# Revit family: Domotics-DomesticRanges-GEWISS-SYSTEM_COMMAND-TWO-WAY_SWITCH_2M
name_source: partatom
category: Apparecchi elettrici
revit_build: Autodesk Revit 2016 (Build: 20161004_0715(x64)
units: mm (PartAtom-declared; Revit-internal decimal feet)

## family parameters
Condiviso = Sì
Host = Superficie
Mantenere orientamento annotazione = Sì
Numero OmniClass = 23.80.50.11.14
Punto di calcolo locali = Sì
Quota connettore circolare = Usa diametro
Taglio con vuoti quando caricato = No
Tipo di parte = Normale
Titolo OmniClass = Switches

## types (2) — shared parameters
Button key = With diffuser
Carico apparente = 0 VA
Catalogue = DOMOTICS
Catalogue Range = SYSTEM - DOMESTIC RANGE
Description. = Two-way switch
Description: = 1P - 16 AX - illuminable
Electrocod = 0130
IDF = 81d0e624-9eec-47de-a259-0ae64e065f3d
IDT = 48717bbd-d383-42eb-95bb-567ea7826302
Immagine tipo = GW21589.jpg
Larghezza pulsante = 46 mm  [stored 0.150919 ft]
N. poli = 1
No. SYSTEM modules = 2
Produttore = GEWISS S.p.A.
Prospetto di default = 1219 mm
SEO = 2 way switch
Simbolo = SIMBOLO DEVIATORI : DEV1P
Technical sheet = https://www.gewiss.com
Tipo_ = SYSTEM DEVIATORI 2M_BASE : Nero
Type = Two-way switch
URL = https://www.gewiss.com
Version file RFA = 19.4
Volt = 230 V
Voltage = 250 V ac
Voltage: = 250 V ac

## per-type parameters (varying)
| type | Colour | Descrizione | EAN code | Modello |
| GW21589 - Black | Black | 2-WAY SWITCH-1P 16AX ILLUM.2M SY/BK | 8011564184619 | GW21589 |
| GW20589 - White | White | 2-WAY SWITCH-1P 16AX ILLUM.2M SY/WT | 8011564184404 | GW20589 |

note: [stored X ft] marks values corroborated as IEEE doubles in the binary element streams (Revit-internal decimal feet)

## geometry (parser evidence)
native form markers: Sweep x1
no freeform markers — native parametric forms only
